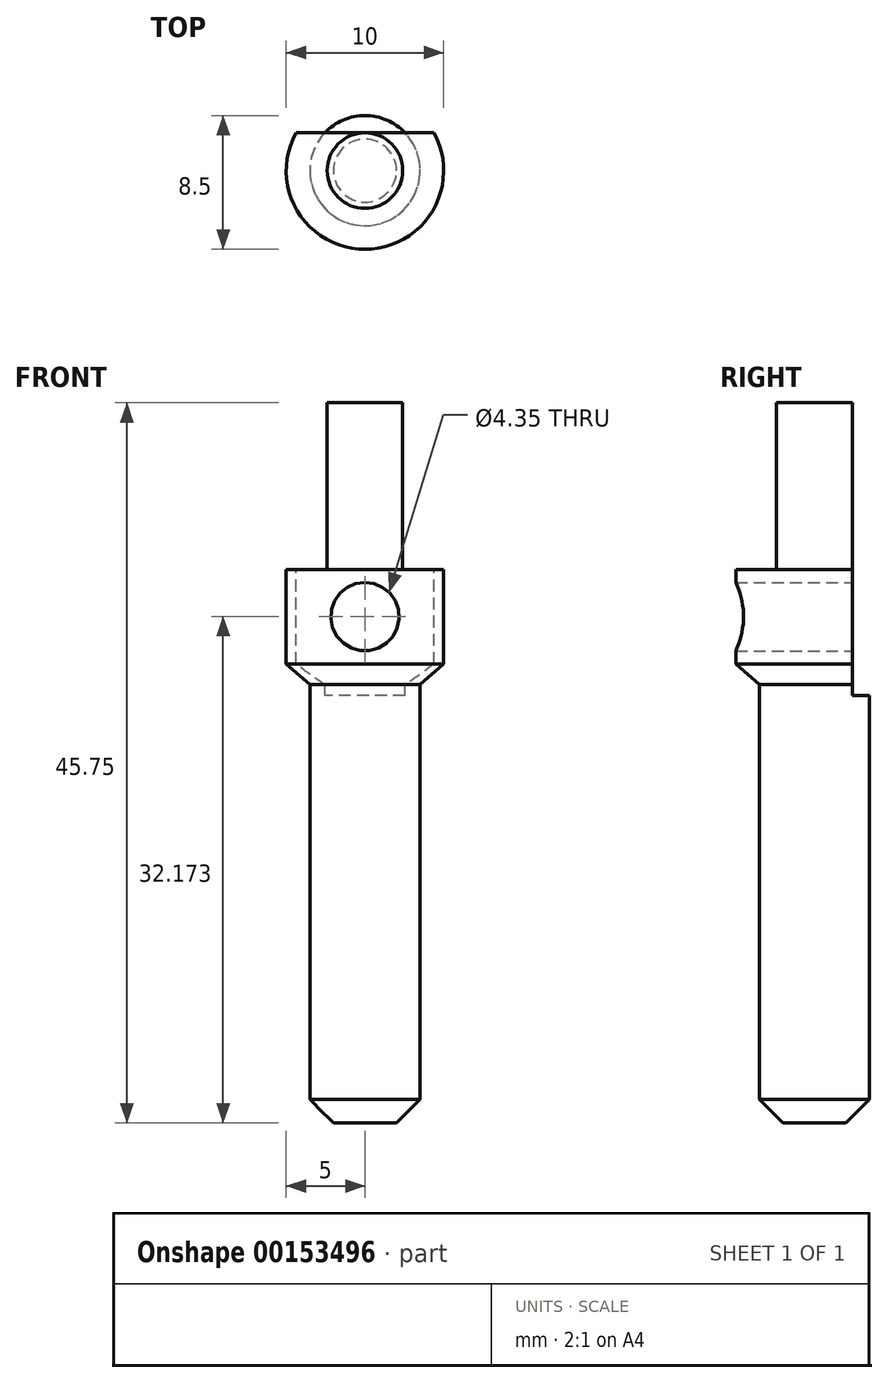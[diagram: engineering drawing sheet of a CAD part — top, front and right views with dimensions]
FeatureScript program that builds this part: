
annotation { "Feature Type Name" : "Feature", "Feature Type Description" : "" }
export const myFeature = defineFeature(function(context is Context, id is Id, definition is map)
    precondition{}
    {
        {
            var Q0;
            Q0=qCreatedBy(makeId("Front.planeOp"),FACE);
            var sketch = newSketch(context, id + "F0", { "sketchPlane" : qUnion([Q0])});
            skLineSegment(sketch, "E0", {"start": v(0, 0) * mm, "end": v(0, 45.75) * mm, "construction": true});
            skLineSegment(sketch, "E1", {"start": v(-3.5, 0) * mm, "end": v(-3.5, 27.85) * mm});
            skPoint(sketch, "E2", {"position": v(-3.5, 27.85) * mm});
            skLineSegment(sketch, "E3", {"start": v(-3.5, 27.85) * mm, "end": v(-5, 29.17) * mm});
            skLineSegment(sketch, "E4", {"start": v(-5, 29.17) * mm, "end": v(-5, 35.17) * mm});
            skLineSegment(sketch, "E5", {"start": v(-5, 35.17) * mm, "end": v(-2.4, 35.17) * mm});
            skLineSegment(sketch, "E6", {"start": v(-2.4, 35.17) * mm, "end": v(-2.4, 45.75) * mm});
            skLineSegment(sketch, "E7", {"start": v(-2.4, 45.75) * mm, "end": v(0, 45.75) * mm});
            skPoint(sketch, "E8.orphan", {"position": v(-3.5, 45.75) * mm});
            skLineSegment(sketch, "E9", {"start": v(-3.5, 0) * mm, "end": v(0, 0) * mm});
            skLineSegment(sketch, "E10", {"start": v(0, 45.75) * mm, "end": v(0, 0) * mm});
            skSolve(sketch);
        }
        {
            var Q0;
            Q0=makeQuery(id+"F0.imprint","IMPRINT",FACE,{"disambiguationData":[TD([[makeQuery(id+"F0.imprint","IMPRINT",EDGE,{"derivedFrom":sQuery(id+"F0.wireOp",EDGE,"E1")}),-1.0]])]});
            var Q1;
            Q1=sQuery(id+"F0.wireOp",EDGE,"E10");
            revolve(context, id + "F1", {"entities" : qUnion([Q0]), "axis" : qUnion([Q1]), "revolveType" : RevolveType.FULL});
        }
        {
            var Q0;
            Q0=makeQuery(id+"F1.opRevolve","SWEPT_EDGE",EDGE,{"disambiguationData":[OSD([sQuery(id+"F0.wireOp",EDGE,"E1"),sQuery(id+"F0.wireOp",EDGE,"E9")])]});
            chamfer(context, id + "F2", {"entities" : qUnion([Q0]), "width" : 1.5 * mm, "tangentPropagation" : true});
        }
        {
            var Q0;
            Q0=makeQuery(id+"F1.opRevolve","SWEPT_FACE",FACE,{"disambiguationData":[OSD([sQuery(id+"F0.wireOp",EDGE,"E5")])]});
            var sketch = newSketch(context, id + "F3", { "sketchPlane" : qUnion([Q0])});
            skLineSegment(sketch, "E11", {"start": v(0, 0) * mm, "end": v(0, 5) * mm, "construction": true});
            skLineSegment(sketch, "E12", {"start": v(0, 2.4) * mm, "end": v(-4.39, 2.4) * mm});
            skLineSegment(sketch, "E13", {"start": v(0, 2.4) * mm, "end": v(4.39, 2.4) * mm});
            skArc(sketch, "E14", {"start": v(4.39, 2.4) * mm, "mid": v(0, 5) * mm, "end": v(-4.39, 2.4) * mm});
            skSolve(sketch);
        }
        {
            var Q0;
            Q0 = qSketchRegion(id + "F3", true);
            extrude(context, id + "F4", {"entities" : qUnion([Q0]), "operationType" : NewBodyOperationType.REMOVE, "oppositeDirection" : true, "depth" : 8 * mm});
        }
        {
            var Q0;
            Q0=makeQuery(id+"F4.boolean.opBoolean","COPY",FACE,{"derivedFrom":makeQuery(id+"F4.opExtrude","SWEPT_FACE",FACE,{"disambiguationData":[OSD([sQuery(id+"F3.wireOp",EDGE,"E12"),sQuery(id+"F3.wireOp",EDGE,"E13")])]})});
            var sketch = newSketch(context, id + "F5", { "sketchPlane" : qUnion([Q0])});
            skPoint(sketch, "E15", {"position": v(0, 32.17) * mm});
            skCircle(sketch, "E16", {"center": v(0, 32.17) * mm, "radius": 2.17 * mm});
            skSolve(sketch);
        }
        {
            var Q0;
            Q0=sQuery(id+"F5.wireOp",VERTEX,"E15");
            var Q1;
            Q1=makeQuery(id+"F1.opRevolve","SWEPT_BODY",BODY,{"disambiguationData":[OSD([sQuery(id+"F0.wireOp",EDGE,"E1"),sQuery(id+"F0.wireOp",EDGE,"E3"),sQuery(id+"F0.wireOp",EDGE,"E4"),sQuery(id+"F0.wireOp",EDGE,"E5"),sQuery(id+"F0.wireOp",EDGE,"E6"),sQuery(id+"F0.wireOp",EDGE,"E7"),sQuery(id+"F0.wireOp",EDGE,"E9"),sQuery(id+"F0.wireOp",EDGE,"E10")])]});
            hole(context, id + "F6", {"style" : HoleStyle.SIMPLE, "endStyle" : HoleEndStyle.THROUGH, "holeDiameter" : 4.35 * mm, "locations" : qUnion([Q0]), "scope" : qUnion([Q1]), "isTappedThrough" : true});
        }
    });
